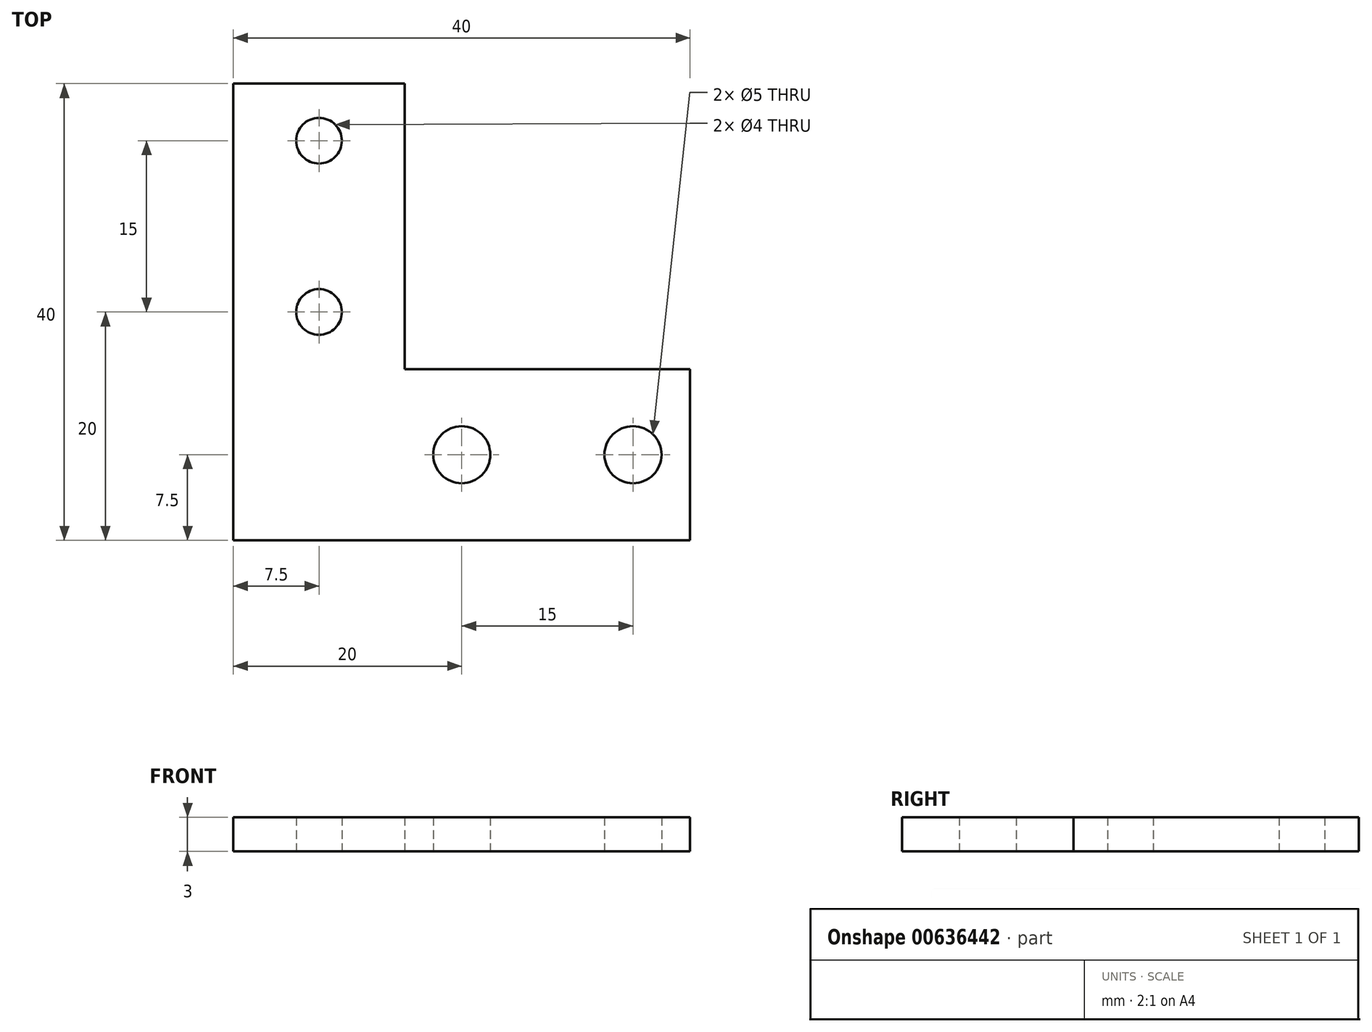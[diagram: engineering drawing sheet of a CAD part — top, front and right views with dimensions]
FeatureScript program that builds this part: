
annotation { "Feature Type Name" : "Feature", "Feature Type Description" : "" }
export const myFeature = defineFeature(function(context is Context, id is Id, definition is map)
    precondition{}
    {
        {
            var Q0;
            Q0=qCreatedBy(makeId("Top.planeOp"),FACE);
            var sketch = newSketch(context, id + "F0", { "sketchPlane" : qUnion([Q0])});
            skLineSegment(sketch, "E0", {"start": v(0, 0) * mm, "end": v(0, 40) * mm});
            skLineSegment(sketch, "E1", {"start": v(0, 40) * mm, "end": v(15, 40) * mm});
            skLineSegment(sketch, "E2", {"start": v(15, 40) * mm, "end": v(15, 15) * mm});
            skLineSegment(sketch, "E3", {"start": v(15, 15) * mm, "end": v(40, 15) * mm});
            skLineSegment(sketch, "E4", {"start": v(40, 15) * mm, "end": v(40, 0) * mm});
            skLineSegment(sketch, "E5", {"start": v(40, 0) * mm, "end": v(0, 0) * mm});
            skCircle(sketch, "E6", {"center": v(7.5, 35) * mm, "radius": 2 * mm});
            skPoint(sketch, "E6.centerSnap0", {"position": v(7.5, 40) * mm});
            skCircle(sketch, "E7", {"center": v(7.5, 20) * mm, "radius": 2 * mm});
            skCircle(sketch, "E8", {"center": v(35, 7.5) * mm, "radius": 2.5 * mm});
            skPoint(sketch, "E8.centerSnap0", {"position": v(40, 7.5) * mm});
            skCircle(sketch, "E9", {"center": v(20, 7.5) * mm, "radius": 2.5 * mm});
            skSolve(sketch);
        }
        {
            var Q0;
            Q0 = qSketchRegion(id + "F0", true);
            extrude(context, id + "F1", {"entities" : qUnion([Q0]), "depth" : 3 * mm, "offsetDistance" : 25 * mm});
        }
    });
